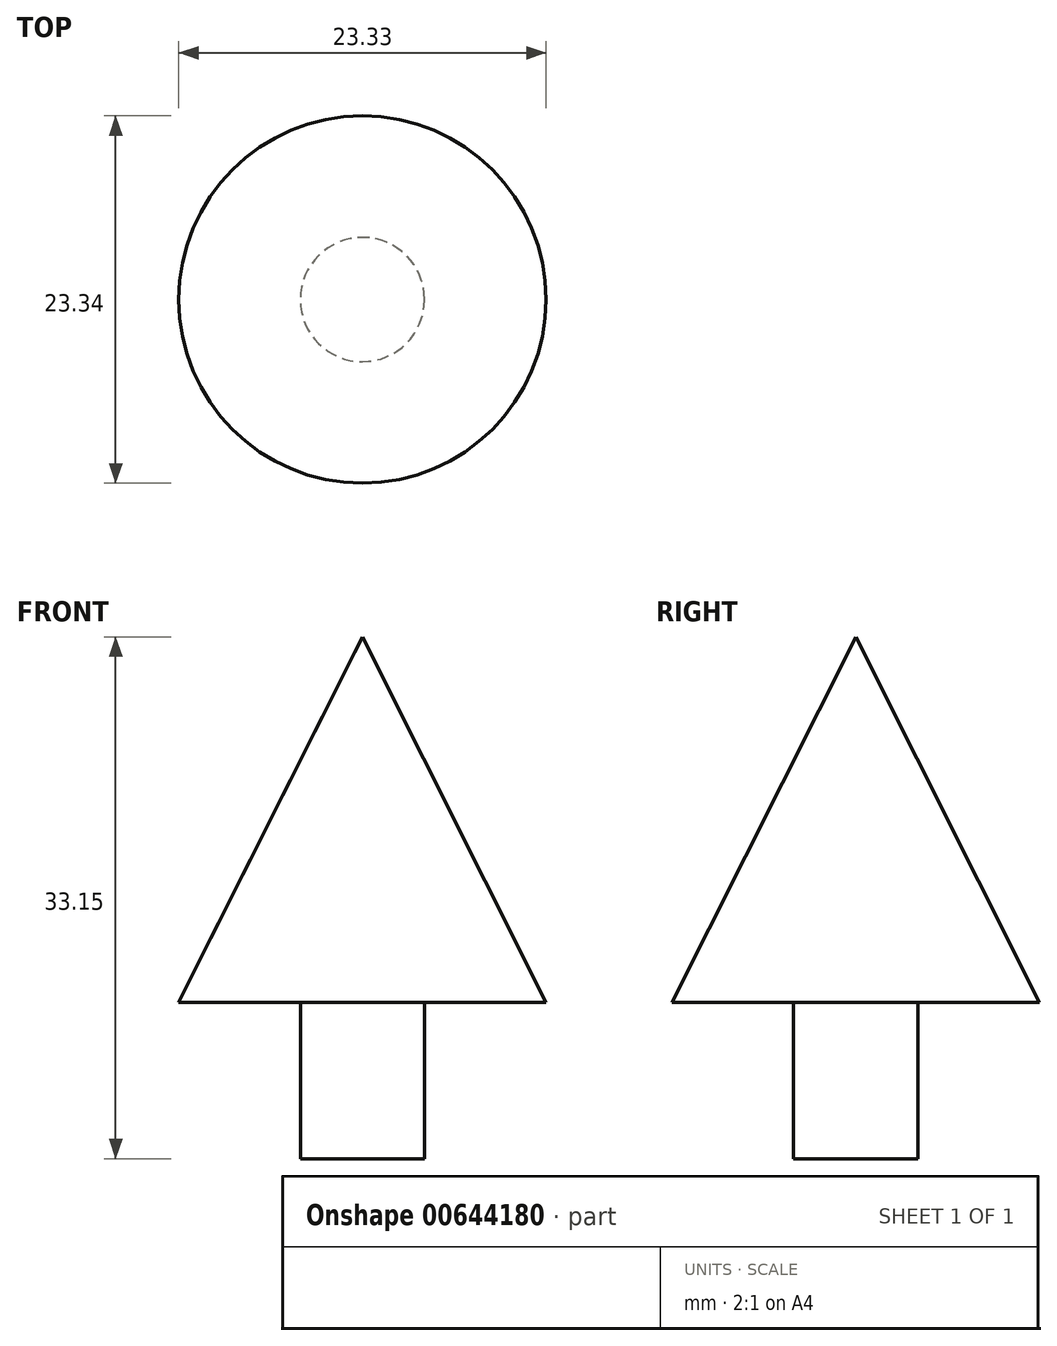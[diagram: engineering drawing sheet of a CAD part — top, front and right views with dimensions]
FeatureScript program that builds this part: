
annotation { "Feature Type Name" : "Feature", "Feature Type Description" : "" }
export const myFeature = defineFeature(function(context is Context, id is Id, definition is map)
    precondition{}
    {
        {
            var Q0;
            Q0=qCreatedBy(makeId("Front.planeOp"),FACE);
            var sketch = newSketch(context, id + "F0", { "sketchPlane" : qUnion([Q0])});
            skLineSegment(sketch, "E0", {"start": v(-23.1, 36.95) * mm, "end": v(-23.1, 3.8) * mm});
            skLineSegment(sketch, "E1", {"start": v(-23.1, 3.8) * mm, "end": v(-27.04, 3.8) * mm});
            skLineSegment(sketch, "E2", {"start": v(-27.04, 3.8) * mm, "end": v(-27.04, 13.74) * mm});
            skLineSegment(sketch, "E3", {"start": v(-27.04, 13.74) * mm, "end": v(-34.76, 13.74) * mm});
            skLineSegment(sketch, "E4", {"start": v(-34.76, 13.74) * mm, "end": v(-23.1, 36.95) * mm});
            skSolve(sketch);
        }
        {
            var Q0;
            Q0=makeQuery(id+"F0.imprint","IMPRINT",FACE,{"disambiguationData":[TD([[makeQuery(id+"F0.imprint","IMPRINT",EDGE,{"derivedFrom":sQuery(id+"F0.wireOp",EDGE,"E0")}),-1.0]])]});
            var Q1;
            Q1=sQuery(id+"F0.wireOp",EDGE,"E0");
            revolve(context, id + "F1", {"entities" : qUnion([Q0]), "axis" : qUnion([Q1]), "revolveType" : RevolveType.FULL});
        }
    });
